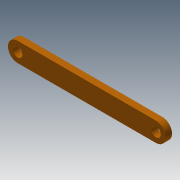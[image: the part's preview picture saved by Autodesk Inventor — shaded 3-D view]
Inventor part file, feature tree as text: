
AUTODESK INVENTOR PART (.ipt)
format: ipt  version: 2015 (Build 190159000, 159)  size: 109,568 bytes
history: native  units: mm
features: extrude x4, sketch x4
ambient origin geometry x8: Origin, YZ Plane, XZ Plane, XY Plane, X Axis, Y Axis, Z Axis, Center Point
bodies: Solid1 (feature_tree)
feature tree (8):
  extrude  "Extrusion1"  Depth=6.0mm
  extrude  "Extrusion2"  Depth=3.0mm
  extrude  "Extrusion3"  Depth=2.0mm TaperAngle=0.0deg
  extrude  "Extrusion4"  Depth=2.0mm
  sketch  "Sketch1"  dims[d0=43.0mm d1=6.0mm]
  sketch  "Sketch2"  dims[d3=2.0mm d4=0.0mm d5=3.0mm]
  sketch  "Sketch3"  dims[d6=3.0mm d7=2.0mm d8=0.0mm]
  sketch  "Sketch4"  dims[d9=0.1mm d10=0.1mm d11=2.0mm d12=0.0mm d13=3.0mm d14=3.0mm d15=2.0mm d16=0.0mm]
